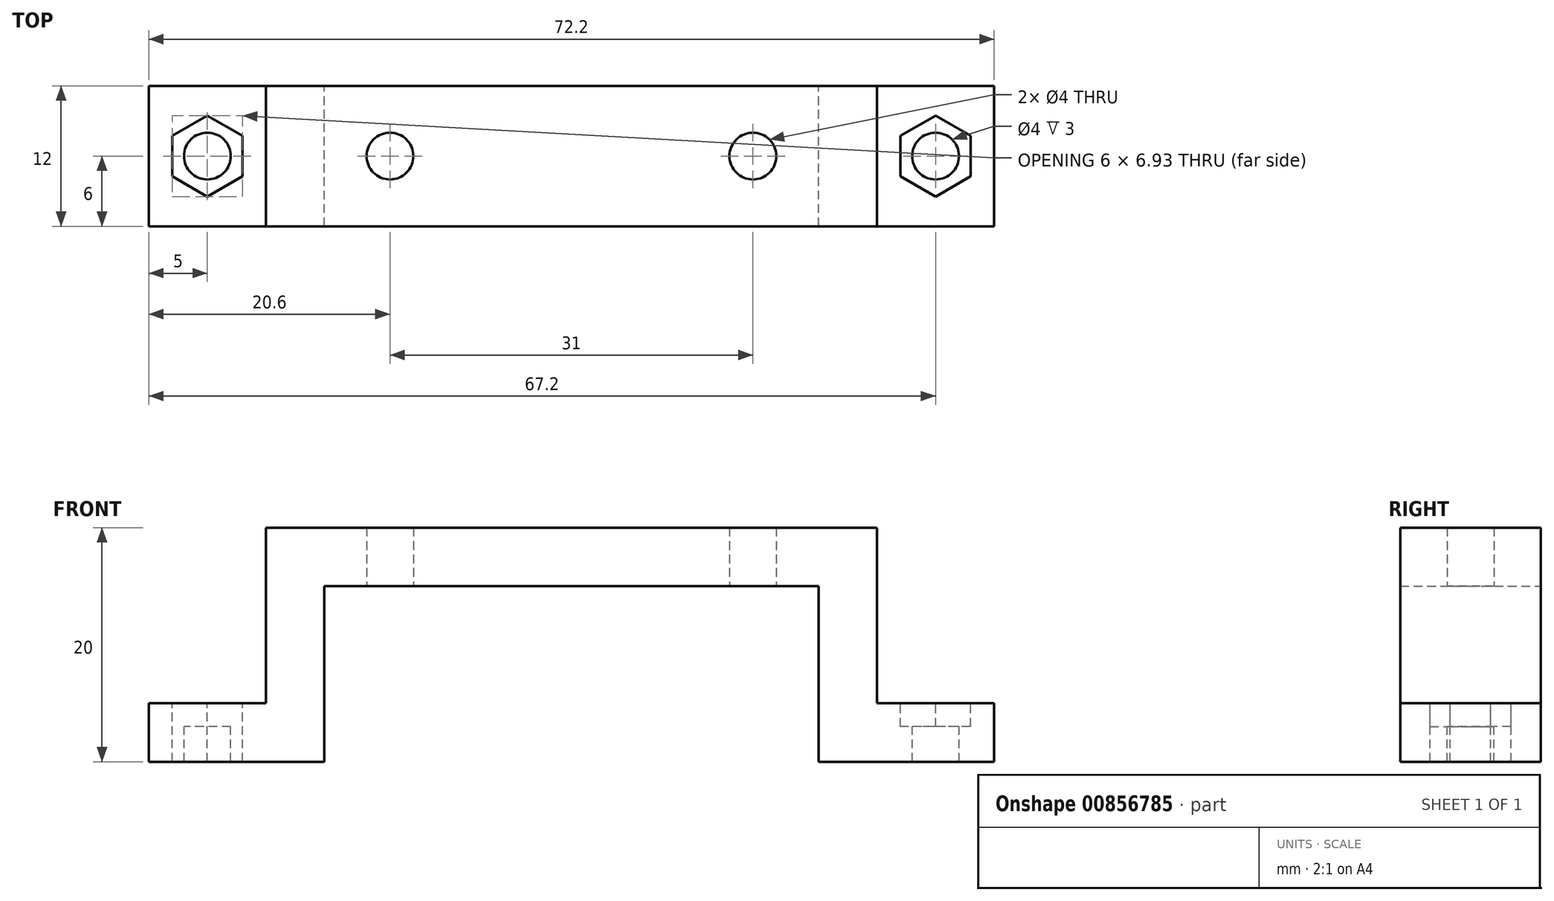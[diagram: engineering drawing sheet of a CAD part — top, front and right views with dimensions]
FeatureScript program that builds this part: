
annotation { "Feature Type Name" : "Feature", "Feature Type Description" : "" }
export const myFeature = defineFeature(function(context is Context, id is Id, definition is map)
    precondition{}
    {
        {
            var Q0;
            Q0=qCreatedBy(makeId("Top.planeOp"),FACE);
            var sketch = newSketch(context, id + "F0", { "sketchPlane" : qUnion([Q0])});
            skLineSegment(sketch, "E0.bottom", {"start": v(21.1, -6) * mm, "end": v(-21.1, -6) * mm});
            skLineSegment(sketch, "E0.top", {"start": v(21.1, 6) * mm, "end": v(-21.1, 6) * mm});
            skLineSegment(sketch, "E0.left", {"start": v(21.1, -6) * mm, "end": v(21.1, 6) * mm});
            skLineSegment(sketch, "E0.right", {"start": v(-21.1, -6) * mm, "end": v(-21.1, 6) * mm});
            skPoint(sketch, "E0.middle", {"position": v(0, 0) * mm});
            skLineSegment(sketch, "E1.bottom", {"start": v(-21.1, 6) * mm, "end": v(-26.1, 6) * mm});
            skLineSegment(sketch, "E1.top", {"start": v(-21.1, -6) * mm, "end": v(-26.1, -6) * mm});
            skLineSegment(sketch, "E1.left", {"start": v(-21.1, 6) * mm, "end": v(-21.1, -6) * mm});
            skLineSegment(sketch, "E1.right", {"start": v(-26.1, 6) * mm, "end": v(-26.1, -6) * mm});
            skLineSegment(sketch, "E2.bottom", {"start": v(21.1, 6) * mm, "end": v(26.1, 6) * mm});
            skLineSegment(sketch, "E2.top", {"start": v(21.1, -6) * mm, "end": v(26.1, -6) * mm});
            skLineSegment(sketch, "E2.left", {"start": v(21.1, 6) * mm, "end": v(21.1, -6) * mm});
            skLineSegment(sketch, "E2.right", {"start": v(26.1, 6) * mm, "end": v(26.1, -6) * mm});
            skCircle(sketch, "E3", {"center": v(15.5, 0) * mm, "radius": 2 * mm});
            skPoint(sketch, "E3.centerSnap0", {"position": v(21.1, 0) * mm});
            skCircle(sketch, "E4", {"center": v(-15.5, 0) * mm, "radius": 2 * mm});
            skSolve(sketch);
        }
        {
            var Q0;
            Q0 = qSketchRegion(id + "F0", true);
            extrude(context, id + "F1", {"entities" : qUnion([Q0]), "depth" : 5 * mm, "offsetDistance" : 25 * mm});
        }
        {
            var Q0;
            Q0=makeQuery(id+"F0.imprint","IMPRINT",FACE,{"disambiguationData":[TD([[makeQuery(id+"F0.imprint","IMPRINT",EDGE,{"derivedFrom":sQuery(id+"F0.wireOp",EDGE,"E2.bottom")}),-1.0]])]});
            var Q1;
            Q1=makeQuery(id+"F0.imprint","IMPRINT",FACE,{"disambiguationData":[TD([[makeQuery(id+"F0.imprint","IMPRINT",EDGE,{"derivedFrom":sQuery(id+"F0.wireOp",EDGE,"E1.bottom")}),1.0]])]});
            extrude(context, id + "F2", {"entities" : qUnion([Q0, Q1]), "operationType" : NewBodyOperationType.ADD, "oppositeDirection" : true, "depth" : 15 * mm, "offsetDistance" : 25 * mm});
        }
        {
            var Q0;
            {var subQ0=sQuery(id+"F0.wireOp",EDGE,"E1.right");Q0=makeQuery(id+"F2.boolean.opBoolean","MERGE",FACE,{"derivedFrom":[makeQuery(id+"F1.opExtrude","SWEPT_FACE",FACE,{"disambiguationData":[OSD([subQ0])]}),makeQuery(id+"F2.opExtrude","SWEPT_FACE",FACE,{"disambiguationData":[OSD([subQ0])]})]});}
            var sketch = newSketch(context, id + "F3", { "sketchPlane" : qUnion([Q0])});
            skLineSegment(sketch, "E5", {"start": v(-6, -10) * mm, "end": v(6, -10) * mm});
            skSolve(sketch);
        }
        {
            var Q0;
            Q0 = qSketchRegion(id + "F3", true);
            var Q1;
            {var subQ0=sQuery(id+"F3.wireOp",EDGE,"E5");Q1=makeQuery(id+"F3.imprint","IMPRINT",FACE,{"disambiguationData":[TD([[makeQuery(id+"F3.imprint","IMPRINT",EDGE,{"derivedFrom":subQ0}),-1.0]])]});}
            extrude(context, id + "F4", {"entities" : qUnion([Q0, Q1]), "operationType" : NewBodyOperationType.ADD, "depth" : 10 * mm, "offsetDistance" : 25 * mm});
        }
        {
            var Q0;
            {var subQ0=sQuery(id+"F0.wireOp",EDGE,"E2.right");Q0=makeQuery(id+"F2.boolean.opBoolean","MERGE",FACE,{"derivedFrom":[makeQuery(id+"F1.opExtrude","SWEPT_FACE",FACE,{"disambiguationData":[OSD([subQ0])]}),makeQuery(id+"F2.opExtrude","SWEPT_FACE",FACE,{"disambiguationData":[OSD([subQ0])]})]});}
            var sketch = newSketch(context, id + "F5", { "sketchPlane" : qUnion([Q0])});
            skLineSegment(sketch, "E6", {"start": v(-6, -10) * mm, "end": v(6, -10) * mm});
            skSolve(sketch);
        }
        {
            var Q0;
            {var subQ0=sQuery(id+"F5.wireOp",EDGE,"E6");Q0=makeQuery(id+"F5.imprint","IMPRINT",FACE,{"disambiguationData":[TD([[makeQuery(id+"F5.imprint","IMPRINT",EDGE,{"derivedFrom":subQ0}),-1.0]])]});}
            extrude(context, id + "F6", {"entities" : qUnion([Q0]), "operationType" : NewBodyOperationType.ADD, "depth" : 10 * mm, "offsetDistance" : 25 * mm});
        }
        {
            var Q0;
            Q0=makeQuery(id+"F6.opExtrude","SWEPT_FACE",FACE,{"disambiguationData":[OSD([sQuery(id+"F5.wireOp",EDGE,"E6")])]});
            var sketch = newSketch(context, id + "F7", { "sketchPlane" : qUnion([Q0])});
            skCircle(sketch, "E7", {"center": v(31.1, 0) * mm, "radius": 2 * mm});
            skPoint(sketch, "E7.centerSnap0", {"position": v(31.1, 6) * mm});
            skCircle(sketch, "E8.MirrorC", {"center": v(-31.1, 0) * mm, "radius": 2 * mm});
            skCircle(sketch, "E9.cCircle", {"center": v(31.1, 0) * mm, "radius": 3 * mm, "construction": true});
            skLineSegment(sketch, "E9.0", {"start": v(28.1, -1.73) * mm, "end": v(28.1, 1.73) * mm});
            skLineSegment(sketch, "E9.1", {"start": v(28.1, 1.73) * mm, "end": v(31.1, 3.46) * mm});
            skLineSegment(sketch, "E9.2", {"start": v(31.1, 3.46) * mm, "end": v(34.1, 1.73) * mm});
            skLineSegment(sketch, "E9.3", {"start": v(34.1, 1.73) * mm, "end": v(34.1, -1.73) * mm});
            skLineSegment(sketch, "E9.4", {"start": v(34.1, -1.73) * mm, "end": v(31.1, -3.46) * mm});
            skLineSegment(sketch, "E9.5", {"start": v(31.1, -3.46) * mm, "end": v(28.1, -1.73) * mm});
            skPoint(sketch, "E9.0.midPoint", {"position": v(28.1, 0) * mm});
            skLineSegment(sketch, "E10.MirrorCS", {"start": v(-31.1, -3.46) * mm, "end": v(-28.1, -1.73) * mm});
            skLineSegment(sketch, "E11.MirrorCS", {"start": v(-34.1, -1.73) * mm, "end": v(-31.1, -3.46) * mm});
            skCircle(sketch, "E12.MirrorC", {"center": v(-31.1, 0) * mm, "radius": 3 * mm, "construction": true});
            skLineSegment(sketch, "E13.MirrorCS", {"start": v(-34.1, 1.73) * mm, "end": v(-34.1, -1.73) * mm});
            skLineSegment(sketch, "E14.MirrorCS", {"start": v(-31.1, 3.46) * mm, "end": v(-34.1, 1.73) * mm});
            skLineSegment(sketch, "E15.MirrorCS", {"start": v(-28.1, 1.73) * mm, "end": v(-31.1, 3.46) * mm});
            skLineSegment(sketch, "E16.MirrorCS", {"start": v(-28.1, -1.73) * mm, "end": v(-28.1, 1.73) * mm});
            skSolve(sketch);
        }
        {
            var Q0;
            Q0=makeQuery(id+"F7.imprint","IMPRINT",FACE,{"disambiguationData":[TD([[makeQuery(id+"F7.imprint","IMPRINT",EDGE,{"derivedFrom":sQuery(id+"F7.wireOp",EDGE,"E7")}),1.0]])]});
            var Q1;
            Q1=makeQuery(id+"F7.imprint","IMPRINT",FACE,{"disambiguationData":[TD([[makeQuery(id+"F7.imprint","IMPRINT",EDGE,{"derivedFrom":sQuery(id+"F7.wireOp",EDGE,"E8.MirrorC")}),-1.0]])]});
            extrude(context, id + "F8", {"entities" : qUnion([Q0, Q1]), "operationType" : NewBodyOperationType.REMOVE, "oppositeDirection" : true, "depth" : 5 * mm, "offsetDistance" : 25 * mm});
        }
        {
            var Q0;
            Q0=makeQuery(id+"F7.imprint","IMPRINT",FACE,{"disambiguationData":[TD([[makeQuery(id+"F7.imprint","IMPRINT",EDGE,{"derivedFrom":sQuery(id+"F7.wireOp",EDGE,"E7")}),-1.0]])]});
            var Q1;
            Q1=makeQuery(id+"F7.imprint","IMPRINT",FACE,{"disambiguationData":[TD([[makeQuery(id+"F7.imprint","IMPRINT",EDGE,{"derivedFrom":sQuery(id+"F7.wireOp",EDGE,"E8.MirrorC")}),1.0]])]});
            extrude(context, id + "F9", {"entities" : qUnion([Q0, Q1]), "operationType" : NewBodyOperationType.REMOVE, "oppositeDirection" : true, "depth" : 2 * mm, "offsetDistance" : 25 * mm});
        }
    });
